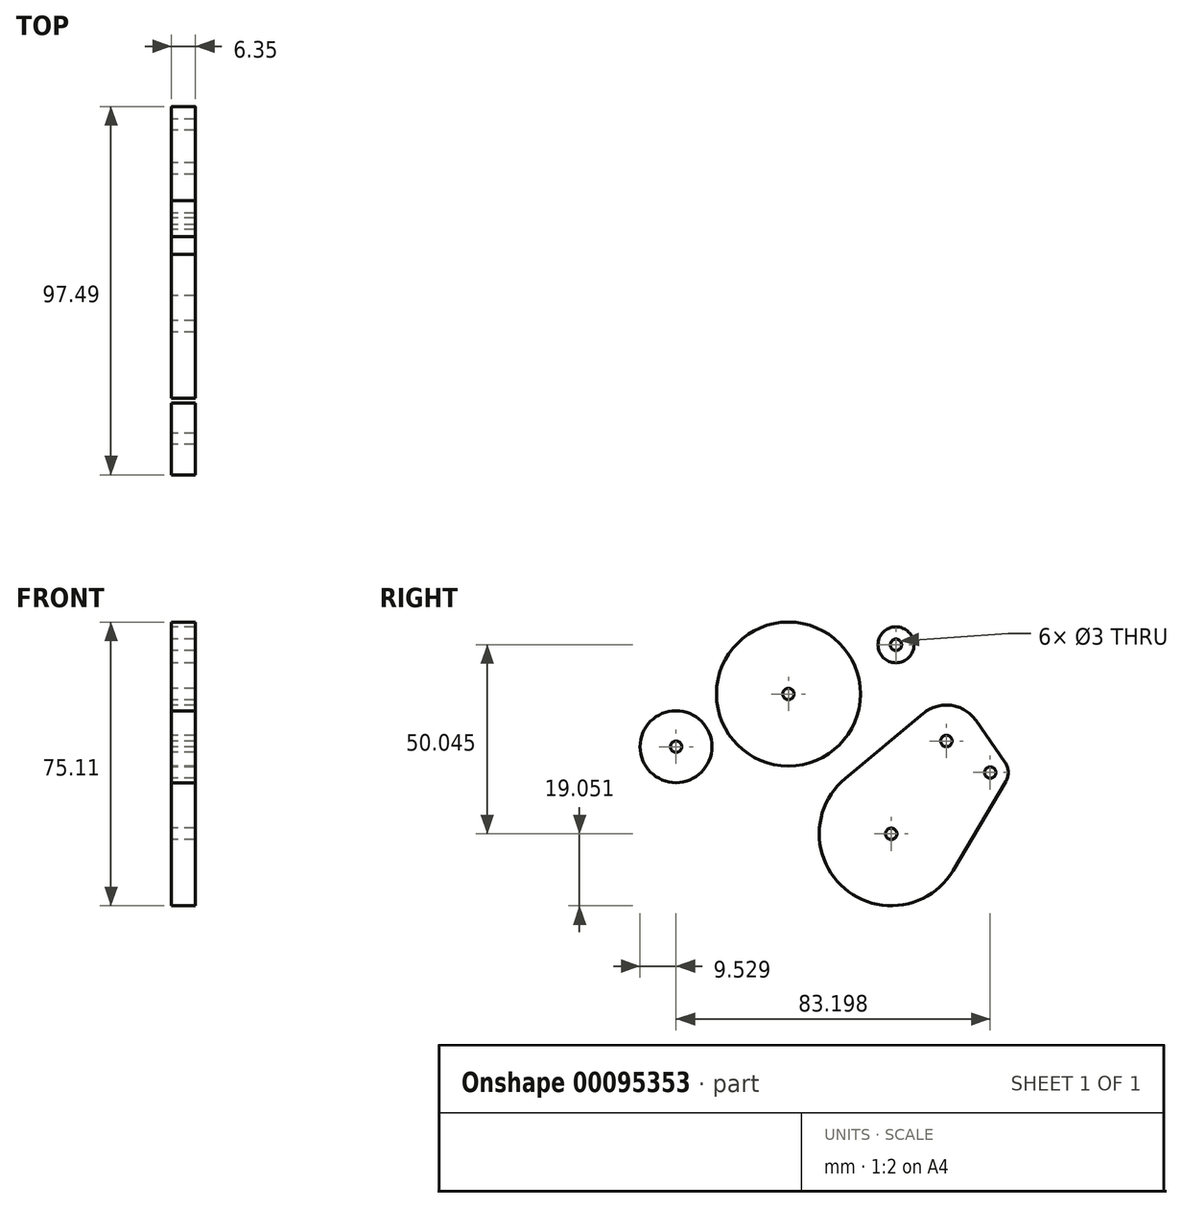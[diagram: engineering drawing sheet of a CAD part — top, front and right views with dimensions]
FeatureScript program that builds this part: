
annotation { "Feature Type Name" : "Feature", "Feature Type Description" : "" }
export const myFeature = defineFeature(function(context is Context, id is Id, definition is map)
    precondition{}
    {
        {
            var Q0;
            Q0=qCreatedBy(makeId("Right.planeOp"),FACE);
            var sketch = newSketch(context, id + "F0", { "sketchPlane" : qUnion([Q0])});
            skArc(sketch, "E0", {"start": v(-7.06, 29.74) * mm, "mid": v(-6.4, 32.34) * mm, "end": v(-7.25, 34.9) * mm});
            skArc(sketch, "E1", {"start": v(-49.56, 30.58) * mm, "mid": v(-49.72, 1.44) * mm, "end": v(-20.98, 6.23) * mm});
            skArc(sketch, "E2", {"start": v(-14.94, 45.94) * mm, "mid": v(-21.49, 49.94) * mm, "end": v(-28.86, 47.82) * mm});
            skCircle(sketch, "E3", {"center": v(-94.35, 39) * mm, "radius": 9.53 * mm});
            skCircle(sketch, "E4", {"center": v(-64.59, 52.95) * mm, "radius": 19.05 * mm});
            skCircle(sketch, "E5", {"center": v(-36.1, 65.99) * mm, "radius": 4.76 * mm});
            skLineSegment(sketch, "E6", {"start": v(-14.94, 45.94) * mm, "end": v(-7.25, 34.9) * mm});
            skLineSegment(sketch, "E7", {"start": v(-20.98, 6.23) * mm, "end": v(-7.06, 29.74) * mm});
            skLineSegment(sketch, "E8", {"start": v(-49.56, 30.58) * mm, "end": v(-28.86, 47.82) * mm});
            skPoint(sketch, "E9.orphan", {"position": v(0, 71.85) * mm});
            skCircle(sketch, "E10", {"center": v(-64.59, 52.95) * mm, "radius": 1.5 * mm});
            skCircle(sketch, "E11", {"center": v(-36.1, 65.99) * mm, "radius": 1.5 * mm});
            skCircle(sketch, "E12", {"center": v(-94.35, 39) * mm, "radius": 1.5 * mm});
            skCircle(sketch, "E13", {"center": v(-37.37, 15.94) * mm, "radius": 1.5 * mm});
            skCircle(sketch, "E14", {"center": v(-22.76, 40.5) * mm, "radius": 1.5 * mm});
            skCircle(sketch, "E15", {"center": v(-11.15, 32.17) * mm, "radius": 1.5 * mm});
            skSolve(sketch);
        }
        {
            var Q0;
            Q0=qSketchRegion(id+"F0",true);
            extrude(context, id + "F1", {"entities" : qUnion([Q0]), "depth" : 6.35 * mm});
        }
    });
